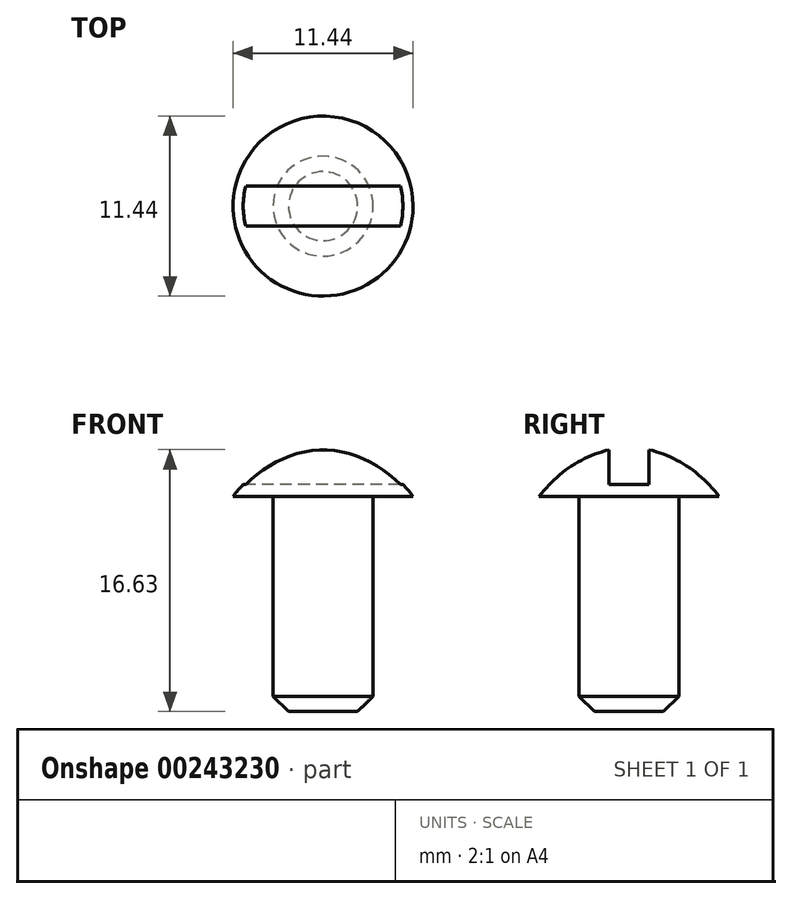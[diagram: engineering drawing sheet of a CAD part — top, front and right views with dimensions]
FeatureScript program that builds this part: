
annotation { "Feature Type Name" : "Feature", "Feature Type Description" : "" }
export const myFeature = defineFeature(function(context is Context, id is Id, definition is map)
    precondition{}
    {
        {
            var Q0;
            Q0=qCreatedBy(makeId("Front.planeOp"),FACE);
            var sketch = newSketch(context, id + "F0", { "sketchPlane" : qUnion([Q0])});
            skLineSegment(sketch, "E0", {"start": v(0, 15.88) * mm, "end": v(0, 0) * mm});
            skLineSegment(sketch, "E1", {"start": v(3.17, 0) * mm, "end": v(3.17, 12.7) * mm});
            skLineSegment(sketch, "E2", {"start": v(3.17, 12.7) * mm, "end": v(5.71, 12.7) * mm});
            skArc(sketch, "E3.trimOffspring", {"start": v(5.71, 12.7) * mm, "mid": v(3.2, 14.9) * mm, "end": v(0, 15.88) * mm});
            skPoint(sketch, "E4.center.orphan", {"position": v(0, 7.94) * mm});
            skPoint(sketch, "E5.end.orphan", {"position": v(0, 12.7) * mm});
            skLineSegment(sketch, "E6", {"start": v(3.18, 0) * mm, "end": v(2.19, -0.96) * mm});
            skLineSegment(sketch, "E7", {"start": v(2.19, -0.96) * mm, "end": v(0, -0.96) * mm});
            skLineSegment(sketch, "E8", {"start": v(0, -0.96) * mm, "end": v(0, 0) * mm});
            skSolve(sketch);
        }
        {
            var Q0;
            Q0=makeQuery(id+"F0.imprint","IMPRINT",FACE,{"disambiguationData":[TD([[makeQuery(id+"F0.imprint","IMPRINT",EDGE,{"derivedFrom":sQuery(id+"F0.wireOp",EDGE,"E0")}),1.0]])]});
            var Q1;
            Q1=sQuery(id+"F0.wireOp",EDGE,"E0");
            revolve(context, id + "F1", {"entities" : qUnion([Q0]), "axis" : qUnion([Q1]), "revolveType" : RevolveType.FULL});
        }
        {
            var Q0;
            Q0=makeQuery(id+"F1.opRevolve","SWEPT_FACE",FACE,{"disambiguationData":[OSD([sQuery(id+"F0.wireOp",EDGE,"E2")])]});
            var sketch = newSketch(context, id + "F2", { "sketchPlane" : qUnion([Q0])});
            skLineSegment(sketch, "E9.bottom", {"start": v(5.08, 1.27) * mm, "end": v(-5.08, 1.27) * mm});
            skLineSegment(sketch, "E9.top", {"start": v(5.08, -1.27) * mm, "end": v(-5.08, -1.27) * mm});
            skLineSegment(sketch, "E9.left", {"start": v(5.08, 1.27) * mm, "end": v(5.08, -1.27) * mm});
            skLineSegment(sketch, "E9.right", {"start": v(-5.08, 1.27) * mm, "end": v(-5.08, -1.27) * mm});
            skPoint(sketch, "E9.middle", {"position": v(0, 0) * mm});
            skSolve(sketch);
        }
        {
            var Q0;
            Q0 = qSketchRegion(id + "F2", true);
            extrude(context, id + "F3", {"entities" : qUnion([Q0]), "operationType" : NewBodyOperationType.REMOVE, "oppositeDirection" : true, "depth" : 6.1 * mm, "hasSecondDirection" : true, "secondDirectionOppositeDirection" : true, "secondDirectionDepth" : 0.76 * mm});
        }
    });
